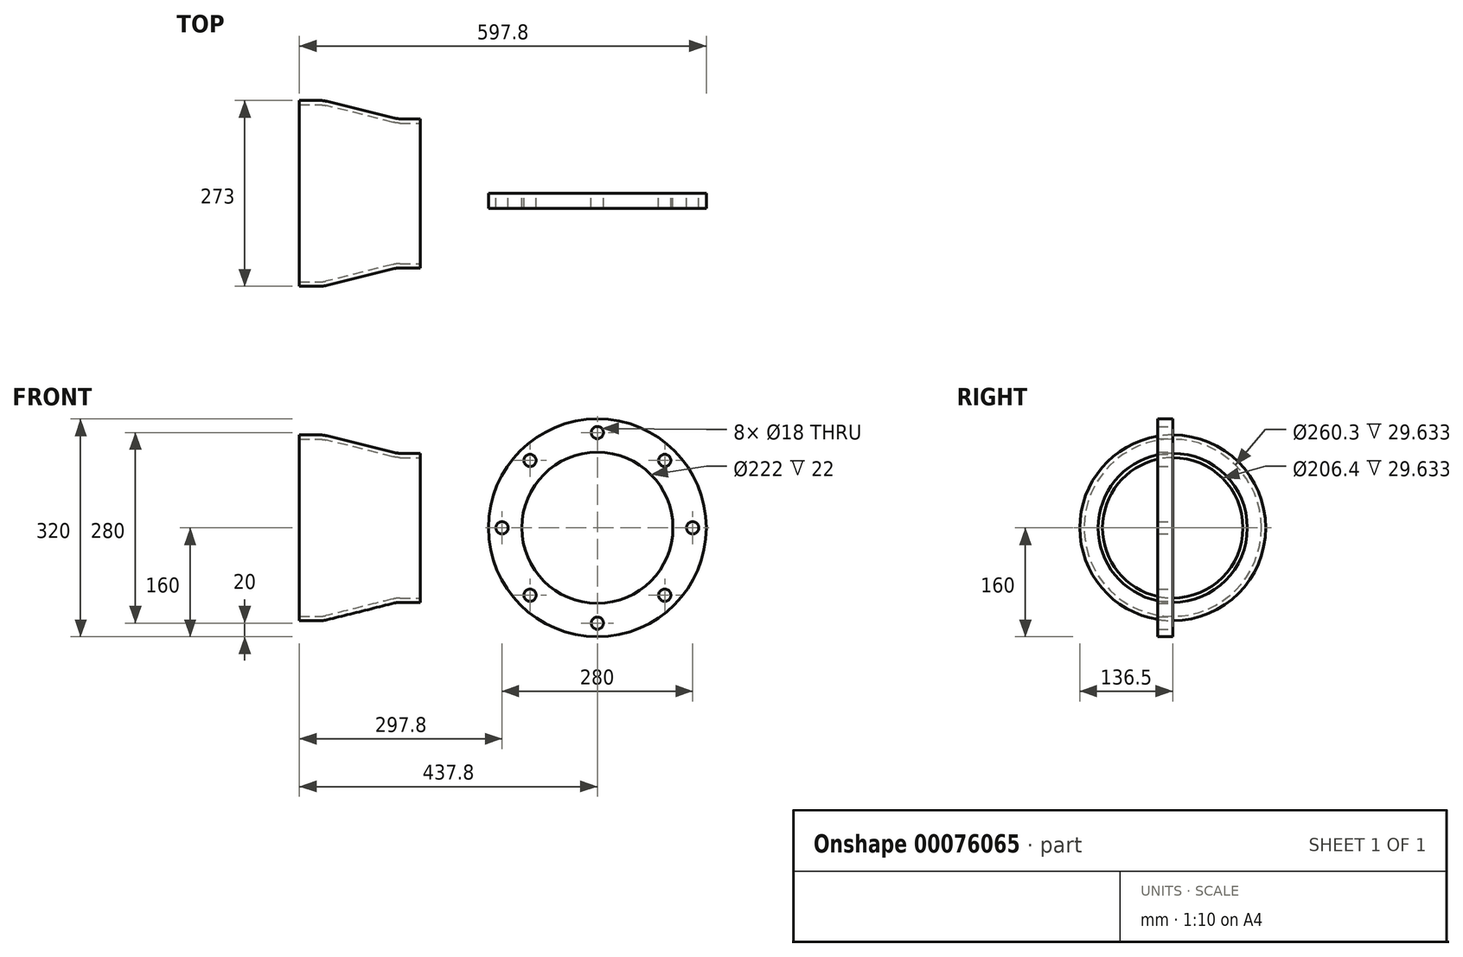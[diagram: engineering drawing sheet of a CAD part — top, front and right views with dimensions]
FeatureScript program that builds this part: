
annotation { "Feature Type Name" : "Feature", "Feature Type Description" : "" }
export const myFeature = defineFeature(function(context is Context, id is Id, definition is map)
    precondition{}
    {
        {
            var Q0;
            Q0=qCreatedBy(makeId("Front.planeOp"),FACE);
            var sketch = newSketch(context, id + "F0", { "sketchPlane" : qUnion([Q0])});
            skLineSegment(sketch, "E0", {"start": v(0, 130.15) * mm, "end": v(0, 136.5) * mm});
            skLineSegment(sketch, "E1", {"start": v(0, 136.5) * mm, "end": v(29.63, 136.5) * mm});
            skLineSegment(sketch, "E2", {"start": v(40.6, 135.16) * mm, "end": v(139.36, 110.63) * mm});
            skLineSegment(sketch, "E3", {"start": v(148.17, 109.55) * mm, "end": v(177.8, 109.55) * mm});
            skLineSegment(sketch, "E4", {"start": v(177.8, 109.55) * mm, "end": v(177.8, 103.2) * mm});
            skLineSegment(sketch, "E5", {"start": v(177.8, 0) * mm, "end": v(0, 0) * mm, "construction": true});
            skLineSegment(sketch, "E6", {"start": v(0, 130.15) * mm, "end": v(29.63, 130.15) * mm});
            skLineSegment(sketch, "E7", {"start": v(39.07, 129) * mm, "end": v(137.83, 104.46) * mm});
            skLineSegment(sketch, "E8", {"start": v(148.17, 103.2) * mm, "end": v(177.8, 103.2) * mm});
            skPoint(sketch, "E9.visualSharp", {"position": v(35.2, 136.5) * mm});
            skArc(sketch, "E9.filletArc", {"start": v(40.6, 135.16) * mm, "mid": v(35.16, 136.16) * mm, "end": v(29.63, 136.5) * mm});
            skPoint(sketch, "E10.visualSharp", {"position": v(34.42, 130.15) * mm});
            skArc(sketch, "E10.filletArc", {"start": v(39.07, 129) * mm, "mid": v(34.39, 129.86) * mm, "end": v(29.63, 130.15) * mm});
            skPoint(sketch, "E11.visualSharp", {"position": v(143.7, 109.55) * mm});
            skArc(sketch, "E11.filletArc", {"start": v(139.36, 110.63) * mm, "mid": v(143.73, 109.82) * mm, "end": v(148.17, 109.55) * mm});
            skPoint(sketch, "E12.visualSharp", {"position": v(142.92, 103.2) * mm});
            skArc(sketch, "E12.filletArc", {"start": v(137.83, 104.46) * mm, "mid": v(142.96, 103.52) * mm, "end": v(148.17, 103.2) * mm});
            skSolve(sketch);
        }
        {
            var Q0;
            Q0=makeQuery(id+"F0.imprint","IMPRINT",FACE,{"disambiguationData":[TD([[makeQuery(id+"F0.imprint","IMPRINT",EDGE,{"derivedFrom":sQuery(id+"F0.wireOp",EDGE,"E0")}),-1.0]])]});
            var Q1;
            Q1=sQuery(id+"F0.wireOp",EDGE,"E5");
            revolve(context, id + "F1", {"entities" : qUnion([Q0]), "axis" : qUnion([Q1]), "revolveType" : RevolveType.FULL});
        }
        {
            assignVariable(context, id + "F2", {"name" : "B9", "anyValue" : 22});
        }
        {
            assignVariable(context, id + "F3", {"name" : "B11", "anyValue" : 8});
        }
        {
            var Q0;
            Q0=qCreatedBy(makeId("Front.planeOp"),FACE);
            var sketch = newSketch(context, id + "F4", { "sketchPlane" : qUnion([Q0])});
            skCircle(sketch, "E13", {"center": v(437.8, 0) * mm, "radius": 160 * mm});
            skCircle(sketch, "E14", {"center": v(437.8, 0) * mm, "radius": 140 * mm, "construction": true});
            skCircle(sketch, "E15", {"center": v(437.8, 0) * mm, "radius": 111 * mm});
            skCircle(sketch, "E16", {"center": v(437.8, 140) * mm, "radius": 9 * mm});
            skSolve(sketch);
        }
        {
            var Q0;
            Q0=makeQuery(id+"F4.imprint","IMPRINT",FACE,{"disambiguationData":[TD([[makeQuery(id+"F4.imprint","IMPRINT",EDGE,{"derivedFrom":sQuery(id+"F4.wireOp",EDGE,"E13")}),1.0]])]});
            extrude(context, id + "F5", {"entities" : qUnion([Q0]), "depth" : (getVariable(context, 'B9')) * mm});
        }
        {
            var Q0;
            Q0=makeQuery(id+"F5.opExtrude","SWEPT_FACE",FACE,{"disambiguationData":[OSD([sQuery(id+"F4.wireOp",EDGE,"E16")])]});
            var Q1;
            Q1=makeQuery(id+"F5.opExtrude","CAP_EDGE",EDGE,{"disambiguationData":[OSD([sQuery(id+"F4.wireOp",EDGE,"E15")])],"isStart":false});
            circularPattern(context, id + "F6", {"patternType" : PatternType.FACE, "faces" : qUnion([Q0]), "axis" : qUnion([Q1]), "angle" : 360 * degree, "instanceCount" : getVariable(context, 'B11'), "equalSpace" : true});
        }
    });
